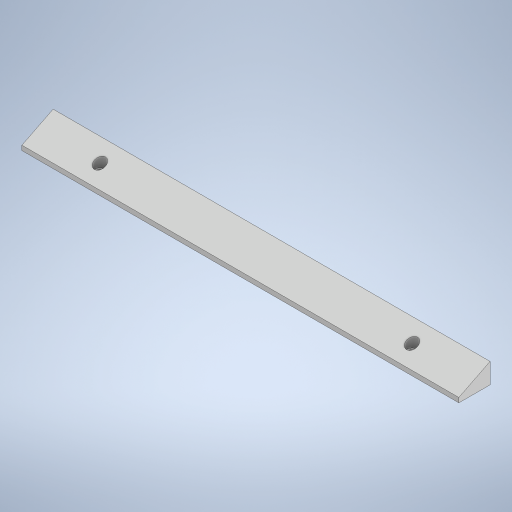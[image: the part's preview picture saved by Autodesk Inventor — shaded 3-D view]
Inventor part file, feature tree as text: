
AUTODESK INVENTOR PART (.ipt)
format: ipt  version: 2023 (Build 270158000, 158)  size: 270,848 bytes
history: native  units: in
note: dims shown in document units (in); Inventor stores cm internally (conversion verified against a paired STEP export)
features: sketch x6, extrude x5
ambient origin geometry x8: Origin, YZ Plane, XZ Plane, XY Plane, X Axis, Y Axis, Z Axis, Center Point
bodies: Solid1 (feature_tree)
feature tree (11):
  extrude  "Extrusion1"  Depth=0.3937in
  extrude  "Extrusion4"  Depth=0.1181in TaperAngle=0.0deg
  sketch  "Sketch7"  dims[d23=0.1693in d24=0.1693in]
  extrude  "Extrusion5"  Depth=0.1693in
  extrude  "Extrusion6"  Depth=0.1181in
  extrude  "Extrusion7"  Depth=0.3937in TaperAngle=0.0deg
  sketch  "Sketch1"  dims[d0=11.0236in d1=0.3937in]
  sketch  "Sketch6"  dims[d2=0.7874in d3=0.0in d21=0.1181in d22=0.0in]
  sketch  "Sketch8"  dims[d25=0.1181in d26=0.0in d27=0.2756in]
  sketch  "Sketch9"  dims[d28=0.2756in d29=0.3937in d30=0.0in]
  sketch  "Sketch10"  dims[d31=0.3937in d32=90.0deg d33=0.0in d34=0.0in d35=7.874in d36=0.3937in d37=0.3937in d38=1.5748in]
